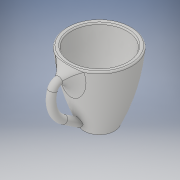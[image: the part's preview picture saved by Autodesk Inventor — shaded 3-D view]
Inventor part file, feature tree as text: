
AUTODESK INVENTOR PART (.ipt)
format: ipt  version: 2017 (Build 210142000, 142)  size: 262,656 bytes
history: native  units: in
note: dims shown in document units (in); Inventor stores cm internally (conversion verified against a paired STEP export)
features: sketch x4, plane x3, revolve x1, sweep x1, fillet x1, chamfer x1
ambient origin geometry x8: Origin, YZ Plane, XZ Plane, XY Plane, X Axis, Y Axis, Z Axis, Center Point
bodies: Solid1 (feature_tree)
feature tree (11):
  revolve  "Revolution1"  [1 undecoded]
  plane  "Work Plane1"
  plane  "Work Plane2"
  sketch  "Sketch3"  dims[d5=0.5in d6=0.0in d7=0.0in d8=0.5in]
  plane  "Work Plane3"
  sweep  "Sweep1"
  sketch  "Sketch5"  dims[d10=1.875in d11=0.125in d12=0.125in d13=45.0deg]
  fillet  "Fillet1"  Radius=0.5in
  chamfer  "Chamfer1"  Distance=0.125in Angle=45.0deg
  sketch  "Sketch1"  dims[d1=90.0deg d2=1.3125in d3=1.625in]
  sketch  "Sketch4"  dims[d9=0.125in]
note: 1 required parameter value undecoded (feature->parameter linkage not recoverable at this tier; creation-order binding heuristic only, values carry confidence <= 0.55)
